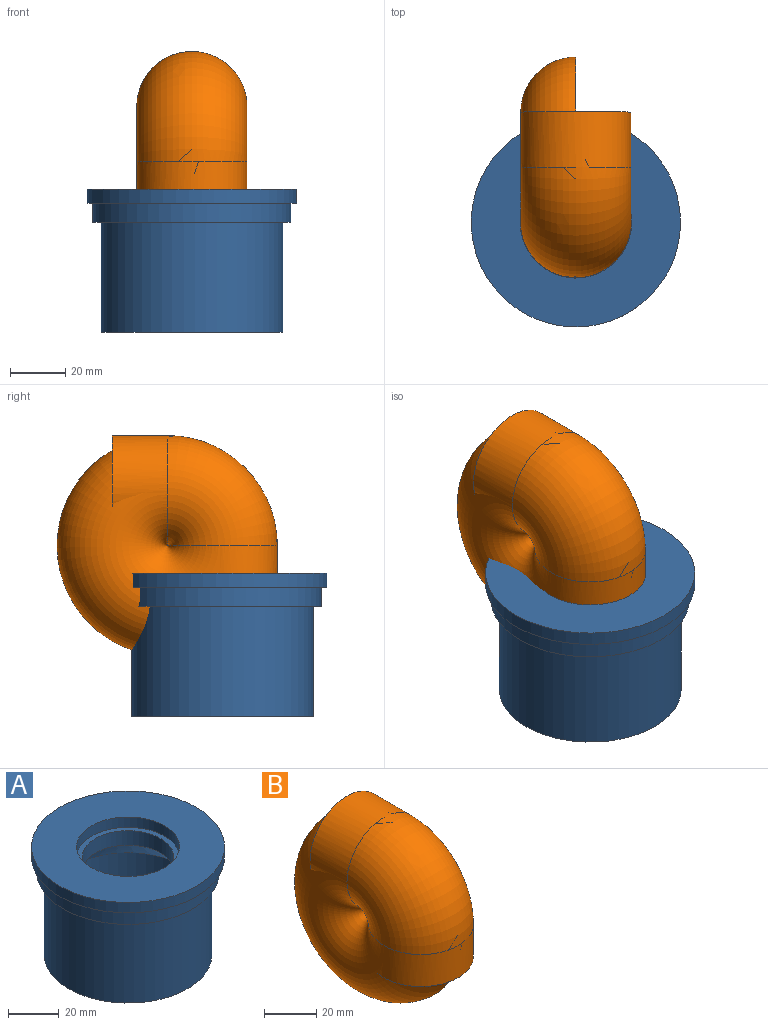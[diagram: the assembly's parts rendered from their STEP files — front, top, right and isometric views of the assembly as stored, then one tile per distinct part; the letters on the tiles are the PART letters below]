
ASSEMBLY  parts=2 mates=1
PART A: 12 faces, bbox 76x76x52 mm
  f0: cylinder r=20.25mm len=40.5mm, axis (0,0,-1), area 636.2mm2, adj f2,f4
  f1: cylinder r=38mm len=76mm, axis (0,0,-1), area 1193.8mm2, adj f2,f3
  f2: plane 76x76mm, normal (0,0,1), area 3248.2mm2, adj f0,f1
  f3: plane 76x76mm, normal (0,0,-1), area 465mm2, adj f1,f5
  f4: plane 40.5x40.5mm, normal (0,0,1), area 270.4mm2, adj f0,f6
  f5: cylinder r=36mm len=72mm, axis (0,0,1), area 1583.4mm2, adj f3,f7
  f6: cylinder r=18mm len=36mm, axis (0,0,1), area 791.7mm2, adj f4,f11
  f7: plane 72x72mm, normal (0,0,-1), area 650.3mm2, adj f5,f9
  f8: cylinder r=30mm len=60mm, axis (0,0,1), area 5277.9mm2, adj f10,f11
  f9: cylinder r=33mm len=66mm, axis (0,0,1), area 8293.8mm2, adj f7,f10
  f10: plane 66x66mm, normal (0,0,-1), area 593.8mm2, adj f8,f9
  f11: cone r=18mm half-angle=45deg, axis (0,0,-1), area 2559.1mm2, adj f6,f8
PART B: 8 faces, bbox 40x86.6x86.6 mm
  f0: cylinder r=18mm len=36mm, axis (0,0,1), area 1696.5mm2, adj f1,f3
  f1: torus R=20mm, axis (-1,0,0), area 3553.1mm2, adj f0,f2
  f2: cylinder r=18mm len=36mm, axis (0,1,0), area 2261.9mm2, adj f1,f4
  f3: plane 40x40mm, normal (0,0,-1), area 238.8mm2, adj f0,f5
  f4: plane 40x40mm, normal (0,1,0), area 238.8mm2, adj f2,f7
  f5: cylinder r=20mm len=40mm, axis (0,0,1), area 1885mm2, adj f3,f6
  f6: torus R=20mm, axis (-1,0,0), area 3947.8mm2, adj f5,f7
  f7: cylinder r=20mm len=40mm, axis (0,1,0), area 2513.3mm2, adj f4,f6
PLACE A t=(-31.63,24.06,25.72)mm
PLACE B t=(-31.63,24.06,-4.28)mm
MATE fastened B.f5 <-> A.f0  axis (0,0,1) through (-31.63,24.06,-4.28)mm
